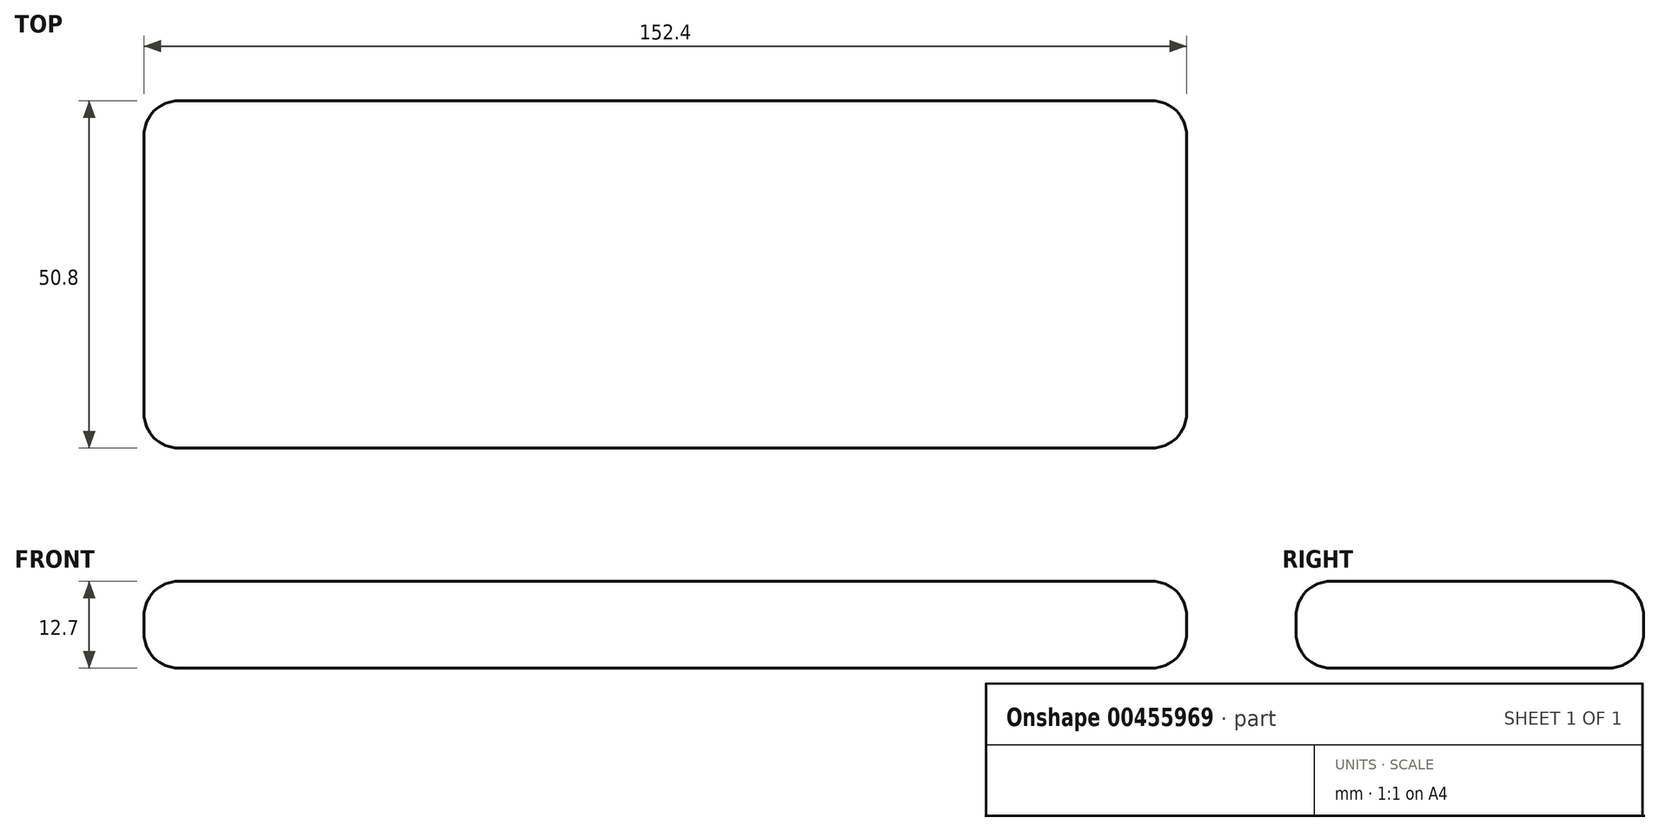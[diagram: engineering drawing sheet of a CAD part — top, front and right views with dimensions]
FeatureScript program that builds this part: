
annotation { "Feature Type Name" : "Feature", "Feature Type Description" : "" }
export const myFeature = defineFeature(function(context is Context, id is Id, definition is map)
    precondition{}
    {
        {
            var Q0;
            Q0=qCreatedBy(makeId("Top.planeOp"),FACE);
            var sketch = newSketch(context, id + "F0", { "sketchPlane" : qUnion([Q0])});
            skLineSegment(sketch, "E0.bottom", {"start": v(-76.2, 25.4) * mm, "end": v(76.2, 25.4) * mm});
            skLineSegment(sketch, "E0.top", {"start": v(-76.2, -25.4) * mm, "end": v(76.2, -25.4) * mm});
            skLineSegment(sketch, "E0.left", {"start": v(-76.2, 25.4) * mm, "end": v(-76.2, -25.4) * mm});
            skLineSegment(sketch, "E0.right", {"start": v(76.2, 25.4) * mm, "end": v(76.2, -25.4) * mm});
            skPoint(sketch, "E0.middle", {"position": v(0, 0) * mm});
            skSolve(sketch);
        }
        {
            var Q0;
            Q0 = qSketchRegion(id + "F0", true);
            extrude(context, id + "F1", {"entities" : qUnion([Q0]), "depth" : 12.7 * mm});
        }
        {
            var Q0;
            Q0=makeQuery(id+"F1.opExtrude","CAP_EDGE",EDGE,{"disambiguationData":[OSD([sQuery(id+"F0.wireOp",EDGE,"E0.top")])],"isStart":false});
            var Q1;
            Q1=makeQuery(id+"F1.opExtrude","SWEPT_EDGE",EDGE,{"disambiguationData":[OSD([sQuery(id+"F0.wireOp",EDGE,"E0.bottom"),sQuery(id+"F0.wireOp",EDGE,"E0.right")])]});
            var Q2;
            Q2=makeQuery(id+"F1.opExtrude","CAP_EDGE",EDGE,{"disambiguationData":[OSD([sQuery(id+"F0.wireOp",EDGE,"E0.right")])],"isStart":false});
            var Q3;
            Q3=makeQuery(id+"F1.opExtrude","CAP_EDGE",EDGE,{"disambiguationData":[OSD([sQuery(id+"F0.wireOp",EDGE,"E0.bottom")])],"isStart":false});
            var Q4;
            Q4=makeQuery(id+"F1.opExtrude","CAP_EDGE",EDGE,{"disambiguationData":[OSD([sQuery(id+"F0.wireOp",EDGE,"E0.left")])],"isStart":false});
            var Q5;
            Q5=makeQuery(id+"F1.opExtrude","SWEPT_EDGE",EDGE,{"disambiguationData":[OSD([sQuery(id+"F0.wireOp",EDGE,"E0.top"),sQuery(id+"F0.wireOp",EDGE,"E0.right")])]});
            var Q6;
            Q6=makeQuery(id+"F1.opExtrude","CAP_EDGE",EDGE,{"disambiguationData":[OSD([sQuery(id+"F0.wireOp",EDGE,"E0.top")])],"isStart":true});
            var Q7;
            Q7=makeQuery(id+"F1.opExtrude","CAP_EDGE",EDGE,{"disambiguationData":[OSD([sQuery(id+"F0.wireOp",EDGE,"E0.right")])],"isStart":true});
            fillet(context, id + "F2", {"entities" : qUnion([Q0, Q1, Q2, Q3, Q4, Q5, Q6, Q7]), "radius" : 5.08 * mm, "tangentPropagation" : true, "allowEdgeOverflow" : false});
        }
        {
            var Q0;
            {var subQ0=sQuery(id+"F0.wireOp",EDGE,"E0.bottom");Q0=makeQuery(id+"F2.opFillet","BLEND_EDGE",EDGE,{"blendedFrom":[makeQuery(id+"F1.opExtrude","CAP_EDGE",EDGE,{"disambiguationData":[OSD([subQ0])],"isStart":false}),makeQuery(id+"F1.opExtrude","SWEPT_FACE",FACE,{"disambiguationData":[OSD([subQ0])]})],"blendedInto":[makeQuery(id+"F1.opExtrude","SWEPT_FACE",FACE,{"disambiguationData":[OSD([subQ0])]})]});}
            var Q1;
            Q1=makeQuery(id+"F1.opExtrude","SWEPT_EDGE",EDGE,{"disambiguationData":[OSD([sQuery(id+"F0.wireOp",EDGE,"E0.top"),sQuery(id+"F0.wireOp",EDGE,"E0.left")])]});
            var Q2;
            Q2=makeQuery(id+"F1.opExtrude","SWEPT_EDGE",EDGE,{"disambiguationData":[OSD([sQuery(id+"F0.wireOp",EDGE,"E0.bottom"),sQuery(id+"F0.wireOp",EDGE,"E0.left")])]});
            var Q3;
            Q3=makeQuery(id+"F1.opExtrude","CAP_EDGE",EDGE,{"disambiguationData":[OSD([sQuery(id+"F0.wireOp",EDGE,"E0.bottom")])],"isStart":true});
            fillet(context, id + "F3", {"entities" : qUnion([Q0, Q1, Q2, Q3]), "radius" : 5.08 * mm, "tangentPropagation" : true, "allowEdgeOverflow" : false});
        }
    });
